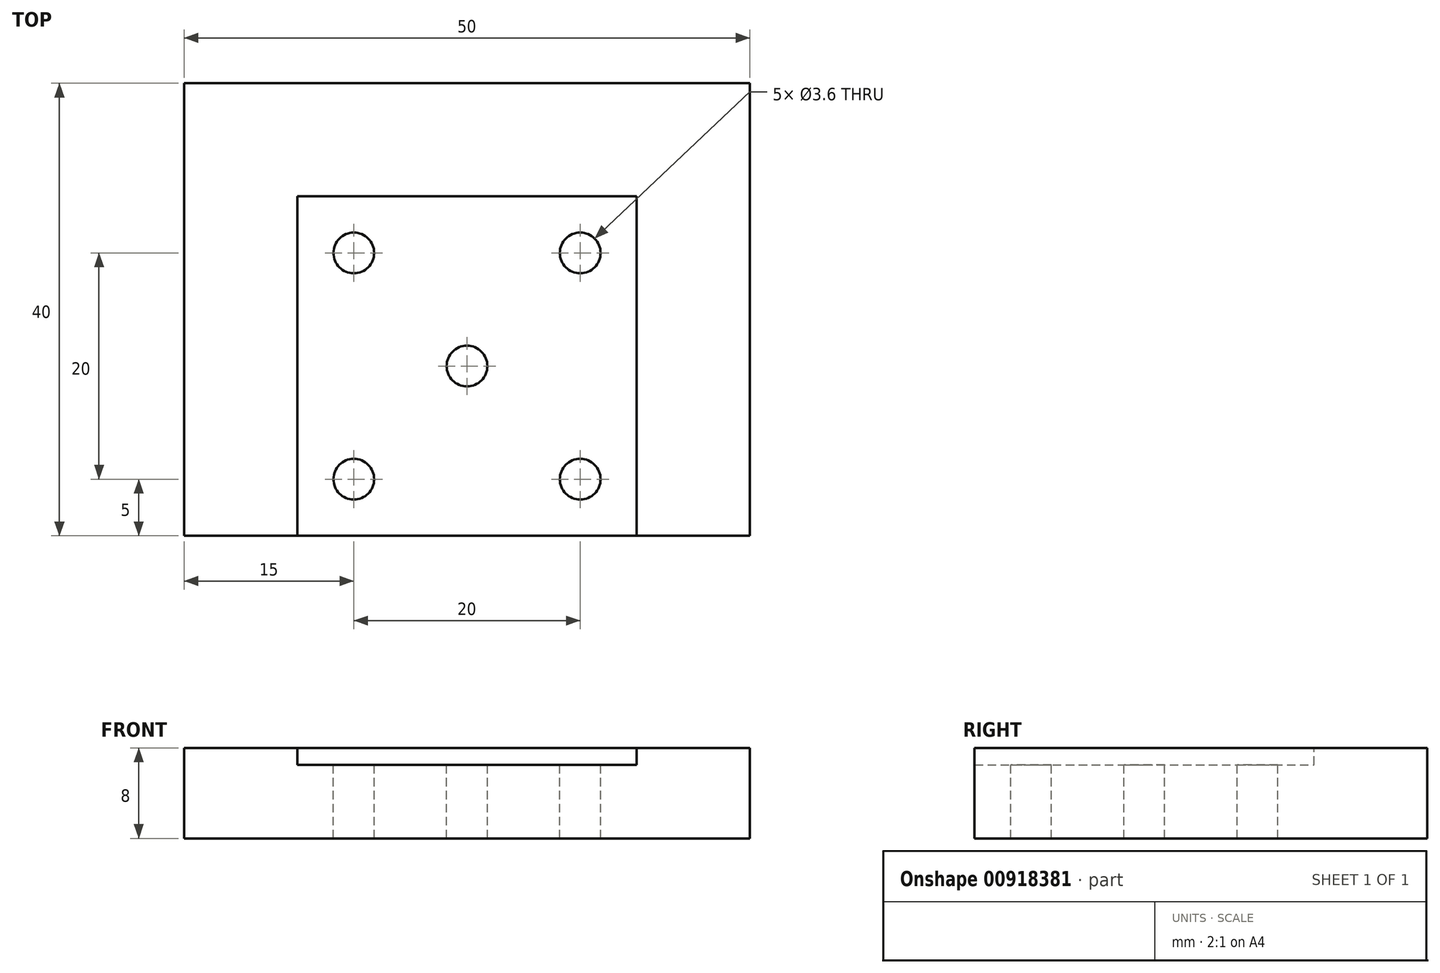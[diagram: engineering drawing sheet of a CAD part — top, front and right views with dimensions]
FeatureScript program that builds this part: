
annotation { "Feature Type Name" : "Feature", "Feature Type Description" : "" }
export const myFeature = defineFeature(function(context is Context, id is Id, definition is map)
    precondition{}
    {
        {
            var Q0;
            Q0=qCreatedBy(makeId("Front.planeOp"),FACE);
            var sketch = newSketch(context, id + "F0", { "sketchPlane" : qUnion([Q0])});
            skCircle(sketch, "E0", {"center": v(0, 18.25) * mm, "radius": 2.85 * mm});
            skCircle(sketch, "E1", {"center": v(0, -18.25) * mm, "radius": 2.85 * mm});
            skCircle(sketch, "E2", {"center": v(0, 0) * mm, "radius": 11 * mm});
            skLineSegment(sketch, "E3", {"start": v(0, 0) * mm, "end": v(0, 18.25) * mm, "construction": true});
            skLineSegment(sketch, "E4", {"start": v(0, -18.25) * mm, "end": v(0, 0) * mm, "construction": true});
            skLineSegment(sketch, "E5.bottom", {"start": v(-15, 28.25) * mm, "end": v(15, 28.25) * mm});
            skLineSegment(sketch, "E5.top", {"start": v(-25, -38.25) * mm, "end": v(25, -38.25) * mm});
            skLineSegment(sketch, "E5.left", {"start": v(-25, 18.25) * mm, "end": v(-25, -38.25) * mm});
            skLineSegment(sketch, "E5.right", {"start": v(25, 18.25) * mm, "end": v(25, -38.25) * mm});
            skLineSegment(sketch, "E6", {"start": v(0, 18.25) * mm, "end": v(0, 28.25) * mm, "construction": true});
            skPoint(sketch, "E7.visualSharp", {"position": v(-25, 28.25) * mm});
            skArc(sketch, "E7.filletArc", {"start": v(-15, 28.25) * mm, "mid": v(-22.07, 25.32) * mm, "end": v(-25, 18.25) * mm});
            skPoint(sketch, "E8.visualSharp", {"position": v(25, 28.25) * mm});
            skArc(sketch, "E8.filletArc", {"start": v(25, 18.25) * mm, "mid": v(22.07, 25.32) * mm, "end": v(15, 28.25) * mm});
            skLineSegment(sketch, "E9", {"start": v(0, 0) * mm, "end": v(25, 0) * mm, "construction": true});
            skSolve(sketch);
        }
        {
            var Q0;
            Q0=makeQuery(id+"F0.imprint","IMPRINT",FACE,{"disambiguationData":[TD([[makeQuery(id+"F0.imprint","IMPRINT",EDGE,{"derivedFrom":sQuery(id+"F0.wireOp",EDGE,"E0")}),-1.0]])]});
            extrude(context, id + "F1", {"entities" : qUnion([Q0]), "depth" : 40 * mm, "offsetDistance" : 25 * mm});
        }
        {
            var Q0;
            Q0=makeQuery(id+"F1.opExtrude","SWEPT_FACE",FACE,{"disambiguationData":[OSD([sQuery(id+"F0.wireOp",EDGE,"E5.bottom")])]});
            var sketch = newSketch(context, id + "F2", { "sketchPlane" : qUnion([Q0])});
            skLineSegment(sketch, "E10.0", {"start": v(-25, -40) * mm, "end": v(-25, 0) * mm, "construction": true});
            skLineSegment(sketch, "E10.1", {"start": v(25, -40) * mm, "end": v(25, 0) * mm, "construction": true});
            skLineSegment(sketch, "E11.bottom", {"start": v(-25, -40) * mm, "end": v(25, -40) * mm});
            skLineSegment(sketch, "E11.top", {"start": v(-25, -10) * mm, "end": v(25, -10) * mm});
            skLineSegment(sketch, "E11.left", {"start": v(-25, -40) * mm, "end": v(-25, -10) * mm});
            skLineSegment(sketch, "E11.right", {"start": v(25, -40) * mm, "end": v(25, -10) * mm});
            skSolve(sketch);
        }
        {
            var Q0;
            {var subQ0=sQuery(id+"F2.wireOp",EDGE,"E11.bottom");var subQ1=sQuery(id+"F0.wireOp",EDGE,"E5.bottom");var subQ2=makeQuery(id+"F1.opExtrude","SWEPT_EDGE",EDGE,{"disambiguationData":[OSD([subQ1,sQuery(id+"F0.wireOp",EDGE,"E7.filletArc")])]});var subQ3=makeQuery(id+"F2.imprint","INTERSECT",VERTEX,{"derivedFrom":[subQ2,subQ0]});Q0=makeQuery(id+"F2.imprint","IMPRINT",FACE,{"disambiguationData":[TD([[makeQuery(id+"F2.imprint","IMPRINT",EDGE,{"disambiguationData":[TD([[subQ3,-1.0]])],"derivedFrom":subQ0}),1.0]])]});}
            extrude(context, id + "F3", {"entities" : qUnion([Q0]), "operationType" : NewBodyOperationType.REMOVE, "oppositeDirection" : true, "depth" : 55 * mm, "offsetDistance" : 25 * mm});
        }
        {
            var Q0;
            Q0=makeQuery(id+"F1.opExtrude","CAP_FACE",FACE,{"disambiguationData":[OSD([sQuery(id+"F0.wireOp",EDGE,"E0"),sQuery(id+"F0.wireOp",EDGE,"E1"),sQuery(id+"F0.wireOp",EDGE,"E2"),sQuery(id+"F0.wireOp",EDGE,"E5.bottom"),sQuery(id+"F0.wireOp",EDGE,"E5.top"),sQuery(id+"F0.wireOp",EDGE,"E5.left"),sQuery(id+"F0.wireOp",EDGE,"E5.right"),sQuery(id+"F0.wireOp",EDGE,"E7.filletArc"),sQuery(id+"F0.wireOp",EDGE,"E8.filletArc")])],"isStart":false});
            var sketch = newSketch(context, id + "F4", { "sketchPlane" : qUnion([Q0])});
            skLineSegment(sketch, "E12.bottom", {"start": v(-15.5, 15.5) * mm, "end": v(15.5, 15.5) * mm, "construction": true});
            skLineSegment(sketch, "E12.top", {"start": v(-15.5, -15.5) * mm, "end": v(15.5, -15.5) * mm, "construction": true});
            skLineSegment(sketch, "E12.left", {"start": v(-15.5, 15.5) * mm, "end": v(-15.5, -15.5) * mm, "construction": true});
            skLineSegment(sketch, "E12.right", {"start": v(15.5, 15.5) * mm, "end": v(15.5, -15.5) * mm, "construction": true});
            skCircle(sketch, "E13", {"center": v(15.5, 15.5) * mm, "radius": 4.5 * mm});
            skCircle(sketch, "E14", {"center": v(-15.5, 15.5) * mm, "radius": 4.5 * mm});
            skCircle(sketch, "E15", {"center": v(-15.5, -15.5) * mm, "radius": 4.5 * mm});
            skCircle(sketch, "E16", {"center": v(15.5, -15.5) * mm, "radius": 4.5 * mm});
            skCircle(sketch, "E17", {"center": v(15.5, 15.5) * mm, "radius": 1.8 * mm});
            skCircle(sketch, "E18", {"center": v(-15.5, 15.5) * mm, "radius": 1.8 * mm});
            skCircle(sketch, "E19", {"center": v(-15.5, -15.5) * mm, "radius": 1.8 * mm});
            skCircle(sketch, "E20", {"center": v(15.5, -15.5) * mm, "radius": 1.8 * mm});
            skSolve(sketch);
        }
        {
            var Q0;
            {var subQ0=sQuery(id+"F4.wireOp",EDGE,"E14");var subQ1=makeQuery(id+"F3.boolean.opBoolean","COPY",EDGE,{"derivedFrom":makeQuery(id+"F3.opExtrude","SWEPT_EDGE",EDGE,{"disambiguationData":[OSD([sQuery(id+"F0.wireOp",EDGE,"E5.bottom"),sQuery(id+"F0.wireOp",EDGE,"E7.filletArc"),sQuery(id+"F2.wireOp",EDGE,"E11.bottom")])]})});var subQ2=makeQuery(id+"F4.imprint","INTERSECT",VERTEX,{"disambiguationData":[OD(0.0)],"derivedFrom":[subQ1,subQ0]});Q0=makeQuery(id+"F4.imprint","IMPRINT",FACE,{"disambiguationData":[TD([[makeQuery(id+"F4.imprint","IMPRINT",EDGE,{"disambiguationData":[TD([[subQ2,1.0]])],"derivedFrom":subQ0}),1.0]])]});}
            var Q1;
            {var subQ0=sQuery(id+"F4.wireOp",EDGE,"E15");var subQ1=makeQuery(id+"F3.boolean.opBoolean","COPY",EDGE,{"derivedFrom":makeQuery(id+"F3.opExtrude","SWEPT_EDGE",EDGE,{"disambiguationData":[OSD([sQuery(id+"F0.wireOp",EDGE,"E5.bottom"),sQuery(id+"F0.wireOp",EDGE,"E7.filletArc"),sQuery(id+"F2.wireOp",EDGE,"E11.bottom")])]})});var subQ2=makeQuery(id+"F4.imprint","INTERSECT",VERTEX,{"disambiguationData":[OD(0.0)],"derivedFrom":[subQ1,subQ0]});Q1=makeQuery(id+"F4.imprint","IMPRINT",FACE,{"disambiguationData":[TD([[makeQuery(id+"F4.imprint","IMPRINT",EDGE,{"disambiguationData":[TD([[subQ2,-1.0]])],"derivedFrom":subQ0}),1.0]])]});}
            var Q2;
            {var subQ0=sQuery(id+"F4.wireOp",EDGE,"E16");var subQ1=makeQuery(id+"F3.boolean.opBoolean","COPY",EDGE,{"derivedFrom":makeQuery(id+"F3.opExtrude","SWEPT_EDGE",EDGE,{"disambiguationData":[OSD([sQuery(id+"F0.wireOp",EDGE,"E5.bottom"),sQuery(id+"F0.wireOp",EDGE,"E8.filletArc"),sQuery(id+"F2.wireOp",EDGE,"E11.bottom")])]})});var subQ2=makeQuery(id+"F4.imprint","INTERSECT",VERTEX,{"disambiguationData":[OD(0.0)],"derivedFrom":[subQ1,subQ0]});Q2=makeQuery(id+"F4.imprint","IMPRINT",FACE,{"disambiguationData":[TD([[makeQuery(id+"F4.imprint","IMPRINT",EDGE,{"disambiguationData":[TD([[subQ2,1.0]])],"derivedFrom":subQ0}),1.0]])]});}
            var Q3;
            {var subQ0=sQuery(id+"F4.wireOp",EDGE,"E13");var subQ1=makeQuery(id+"F3.boolean.opBoolean","COPY",EDGE,{"derivedFrom":makeQuery(id+"F3.opExtrude","SWEPT_EDGE",EDGE,{"disambiguationData":[OSD([sQuery(id+"F0.wireOp",EDGE,"E5.bottom"),sQuery(id+"F0.wireOp",EDGE,"E8.filletArc"),sQuery(id+"F2.wireOp",EDGE,"E11.bottom")])]})});var subQ2=makeQuery(id+"F4.imprint","INTERSECT",VERTEX,{"disambiguationData":[OD(0.0)],"derivedFrom":[subQ1,subQ0]});Q3=makeQuery(id+"F4.imprint","IMPRINT",FACE,{"disambiguationData":[TD([[makeQuery(id+"F4.imprint","IMPRINT",EDGE,{"disambiguationData":[TD([[subQ2,-1.0]])],"derivedFrom":subQ0}),1.0]])]});}
            var Q4;
            Q4=makeQuery(id+"F3.boolean.opBoolean","COPY",VERTEX,{"derivedFrom":makeQuery(id+"F3.opExtrude","CAP_VERTEX",VERTEX,{"disambiguationData":[OSD([sQuery(id+"F0.wireOp",EDGE,"E5.bottom"),sQuery(id+"F0.wireOp",EDGE,"E7.filletArc"),sQuery(id+"F2.wireOp",EDGE,"E11.top")])],"isStart":true})});
            extrude(context, id + "F5", {"entities" : qUnion([Q0, Q1, Q2, Q3]), "operationType" : NewBodyOperationType.ADD, "endBound" : BoundingType.UP_TO_VERTEX, "oppositeDirection" : true, "depth" : 25 * mm, "endBoundEntityVertex" : qUnion([Q4]), "offsetDistance" : 25 * mm});
        }
        {
            var Q0;
            {var subQ0=sQuery(id+"F4.wireOp",EDGE,"E18");var subQ1=makeQuery(id+"F3.boolean.opBoolean","COPY",EDGE,{"derivedFrom":makeQuery(id+"F3.opExtrude","SWEPT_EDGE",EDGE,{"disambiguationData":[OSD([sQuery(id+"F0.wireOp",EDGE,"E5.bottom"),sQuery(id+"F0.wireOp",EDGE,"E7.filletArc"),sQuery(id+"F2.wireOp",EDGE,"E11.bottom")])]})});var subQ2=makeQuery(id+"F4.imprint","INTERSECT",VERTEX,{"disambiguationData":[OD(0.0)],"derivedFrom":[subQ1,subQ0]});Q0=makeQuery(id+"F4.imprint","IMPRINT",FACE,{"disambiguationData":[TD([[makeQuery(id+"F4.imprint","IMPRINT",EDGE,{"disambiguationData":[TD([[subQ2,-1.0]])],"derivedFrom":subQ0}),1.0]])]});}
            var Q1;
            {var subQ0=sQuery(id+"F4.wireOp",EDGE,"E17");var subQ1=makeQuery(id+"F3.boolean.opBoolean","COPY",EDGE,{"derivedFrom":makeQuery(id+"F3.opExtrude","SWEPT_EDGE",EDGE,{"disambiguationData":[OSD([sQuery(id+"F0.wireOp",EDGE,"E5.bottom"),sQuery(id+"F0.wireOp",EDGE,"E8.filletArc"),sQuery(id+"F2.wireOp",EDGE,"E11.bottom")])]})});var subQ2=makeQuery(id+"F4.imprint","INTERSECT",VERTEX,{"disambiguationData":[OD(0.0)],"derivedFrom":[subQ1,subQ0]});Q1=makeQuery(id+"F4.imprint","IMPRINT",FACE,{"disambiguationData":[TD([[makeQuery(id+"F4.imprint","IMPRINT",EDGE,{"disambiguationData":[TD([[subQ2,1.0]])],"derivedFrom":subQ0}),1.0]])]});}
            var Q2;
            {var subQ0=sQuery(id+"F4.wireOp",EDGE,"E20");var subQ1=makeQuery(id+"F3.boolean.opBoolean","COPY",EDGE,{"derivedFrom":makeQuery(id+"F3.opExtrude","SWEPT_EDGE",EDGE,{"disambiguationData":[OSD([sQuery(id+"F0.wireOp",EDGE,"E5.bottom"),sQuery(id+"F0.wireOp",EDGE,"E8.filletArc"),sQuery(id+"F2.wireOp",EDGE,"E11.bottom")])]})});var subQ2=makeQuery(id+"F4.imprint","INTERSECT",VERTEX,{"disambiguationData":[OD(0.0)],"derivedFrom":[subQ1,subQ0]});Q2=makeQuery(id+"F4.imprint","IMPRINT",FACE,{"disambiguationData":[TD([[makeQuery(id+"F4.imprint","IMPRINT",EDGE,{"disambiguationData":[TD([[subQ2,-1.0]])],"derivedFrom":subQ0}),1.0]])]});}
            var Q3;
            {var subQ0=sQuery(id+"F4.wireOp",EDGE,"E19");var subQ1=makeQuery(id+"F3.boolean.opBoolean","COPY",EDGE,{"derivedFrom":makeQuery(id+"F3.opExtrude","SWEPT_EDGE",EDGE,{"disambiguationData":[OSD([sQuery(id+"F0.wireOp",EDGE,"E5.bottom"),sQuery(id+"F0.wireOp",EDGE,"E7.filletArc"),sQuery(id+"F2.wireOp",EDGE,"E11.bottom")])]})});var subQ2=makeQuery(id+"F4.imprint","INTERSECT",VERTEX,{"disambiguationData":[OD(0.0)],"derivedFrom":[subQ1,subQ0]});Q3=makeQuery(id+"F4.imprint","IMPRINT",FACE,{"disambiguationData":[TD([[makeQuery(id+"F4.imprint","IMPRINT",EDGE,{"disambiguationData":[TD([[subQ2,1.0]])],"derivedFrom":subQ0}),1.0]])]});}
            extrude(context, id + "F6", {"entities" : qUnion([Q0, Q1, Q2, Q3]), "operationType" : NewBodyOperationType.REMOVE, "endBound" : BoundingType.THROUGH_ALL, "oppositeDirection" : true, "depth" : 25 * mm, "offsetDistance" : 25 * mm});
        }
        {
            var Q0;
            {var subQ0=sQuery(id+"F4.wireOp",EDGE,"E18");var subQ1=makeQuery(id+"F3.boolean.opBoolean","COPY",EDGE,{"derivedFrom":makeQuery(id+"F3.opExtrude","SWEPT_EDGE",EDGE,{"disambiguationData":[OSD([sQuery(id+"F0.wireOp",EDGE,"E5.bottom"),sQuery(id+"F0.wireOp",EDGE,"E7.filletArc"),sQuery(id+"F2.wireOp",EDGE,"E11.bottom")])]})});var subQ2=makeQuery(id+"F4.imprint","INTERSECT",VERTEX,{"disambiguationData":[OD(0.0)],"derivedFrom":[subQ1,subQ0]});Q0=makeQuery(id+"F4.imprint","IMPRINT",FACE,{"disambiguationData":[TD([[makeQuery(id+"F4.imprint","IMPRINT",EDGE,{"disambiguationData":[TD([[subQ2,1.0]])],"derivedFrom":subQ0}),1.0]])]});}
            var Q1;
            {var subQ0=sQuery(id+"F4.wireOp",EDGE,"E17");var subQ1=makeQuery(id+"F3.boolean.opBoolean","COPY",EDGE,{"derivedFrom":makeQuery(id+"F3.opExtrude","SWEPT_EDGE",EDGE,{"disambiguationData":[OSD([sQuery(id+"F0.wireOp",EDGE,"E5.bottom"),sQuery(id+"F0.wireOp",EDGE,"E8.filletArc"),sQuery(id+"F2.wireOp",EDGE,"E11.bottom")])]})});var subQ2=makeQuery(id+"F4.imprint","INTERSECT",VERTEX,{"disambiguationData":[OD(0.0)],"derivedFrom":[subQ1,subQ0]});Q1=makeQuery(id+"F4.imprint","IMPRINT",FACE,{"disambiguationData":[TD([[makeQuery(id+"F4.imprint","IMPRINT",EDGE,{"disambiguationData":[TD([[subQ2,-1.0]])],"derivedFrom":subQ0}),1.0]])]});}
            var Q2;
            {var subQ0=sQuery(id+"F4.wireOp",EDGE,"E19");var subQ1=makeQuery(id+"F3.boolean.opBoolean","COPY",EDGE,{"derivedFrom":makeQuery(id+"F3.opExtrude","SWEPT_EDGE",EDGE,{"disambiguationData":[OSD([sQuery(id+"F0.wireOp",EDGE,"E5.bottom"),sQuery(id+"F0.wireOp",EDGE,"E7.filletArc"),sQuery(id+"F2.wireOp",EDGE,"E11.bottom")])]})});var subQ2=makeQuery(id+"F4.imprint","INTERSECT",VERTEX,{"disambiguationData":[OD(0.0)],"derivedFrom":[subQ1,subQ0]});Q2=makeQuery(id+"F4.imprint","IMPRINT",FACE,{"disambiguationData":[TD([[makeQuery(id+"F4.imprint","IMPRINT",EDGE,{"disambiguationData":[TD([[subQ2,-1.0]])],"derivedFrom":subQ0}),1.0]])]});}
            var Q3;
            {var subQ0=sQuery(id+"F4.wireOp",EDGE,"E20");var subQ1=makeQuery(id+"F3.boolean.opBoolean","COPY",EDGE,{"derivedFrom":makeQuery(id+"F3.opExtrude","SWEPT_EDGE",EDGE,{"disambiguationData":[OSD([sQuery(id+"F0.wireOp",EDGE,"E5.bottom"),sQuery(id+"F0.wireOp",EDGE,"E8.filletArc"),sQuery(id+"F2.wireOp",EDGE,"E11.bottom")])]})});var subQ2=makeQuery(id+"F4.imprint","INTERSECT",VERTEX,{"disambiguationData":[OD(0.0)],"derivedFrom":[subQ1,subQ0]});Q3=makeQuery(id+"F4.imprint","IMPRINT",FACE,{"disambiguationData":[TD([[makeQuery(id+"F4.imprint","IMPRINT",EDGE,{"disambiguationData":[TD([[subQ2,1.0]])],"derivedFrom":subQ0}),1.0]])]});}
            extrude(context, id + "F7", {"entities" : qUnion([Q0, Q1, Q2, Q3]), "operationType" : NewBodyOperationType.REMOVE, "endBound" : BoundingType.THROUGH_ALL, "oppositeDirection" : true, "depth" : 25 * mm, "offsetDistance" : 25 * mm});
        }
        {
            var Q0;
            Q0=makeQuery(id+"F3.boolean.opBoolean","COPY",FACE,{"derivedFrom":makeQuery(id+"F3.opExtrude","CAP_FACE",FACE,{"disambiguationData":[OSD([sQuery(id+"F0.wireOp",EDGE,"E5.bottom"),sQuery(id+"F0.wireOp",EDGE,"E7.filletArc"),sQuery(id+"F0.wireOp",EDGE,"E8.filletArc"),sQuery(id+"F2.wireOp",EDGE,"E11.bottom"),sQuery(id+"F2.wireOp",EDGE,"E11.top")])],"isStart":false})});
            var sketch = newSketch(context, id + "F8", { "sketchPlane" : qUnion([Q0])});
            skLineSegment(sketch, "E21.bottom", {"start": v(-10, -15) * mm, "end": v(10, -15) * mm, "construction": true});
            skLineSegment(sketch, "E21.top", {"start": v(-10, -35) * mm, "end": v(10, -35) * mm, "construction": true});
            skLineSegment(sketch, "E21.left", {"start": v(-10, -15) * mm, "end": v(-10, -35) * mm, "construction": true});
            skLineSegment(sketch, "E21.right", {"start": v(10, -15) * mm, "end": v(10, -35) * mm, "construction": true});
            skLineSegment(sketch, "E22", {"start": v(-15, -25) * mm, "end": v(15, -25) * mm, "construction": true});
            skCircle(sketch, "E23", {"center": v(-10, -15) * mm, "radius": 1.8 * mm});
            skCircle(sketch, "E24", {"center": v(10, -15) * mm, "radius": 1.8 * mm});
            skCircle(sketch, "E25", {"center": v(-10, -35) * mm, "radius": 1.8 * mm});
            skCircle(sketch, "E26", {"center": v(10, -35) * mm, "radius": 1.8 * mm});
            skCircle(sketch, "E27", {"center": v(0, -25) * mm, "radius": 1.8 * mm});
            skSolve(sketch);
        }
        {
            var Q0;
            Q0=qSketchRegion(id+"F8",true);
            var Q1;
            Q1=makeQuery(id+"F1.opExtrude","SWEPT_FACE",FACE,{"disambiguationData":[OSD([sQuery(id+"F0.wireOp",EDGE,"E5.top")])]});
            extrude(context, id + "F9", {"entities" : qUnion([Q0]), "operationType" : NewBodyOperationType.REMOVE, "endBound" : BoundingType.UP_TO_SURFACE, "oppositeDirection" : true, "depth" : 25 * mm, "endBoundEntityFace" : qUnion([Q1]), "offsetDistance" : 25 * mm});
        }
        {
            var Q0;
            Q0=makeQuery(id+"F1.opExtrude","SWEPT_FACE",FACE,{"disambiguationData":[OSD([sQuery(id+"F0.wireOp",EDGE,"E5.top")])]});
            extrude(context, id + "F10", {"entities" : qUnion([Q0]), "operationType" : NewBodyOperationType.INTERSECT, "oppositeDirection" : true, "depth" : 13 * mm, "offsetDistance" : 25 * mm});
        }
        {
            var Q0;
            Q0=makeQuery(id+"F1.opExtrude","SWEPT_FACE",FACE,{"disambiguationData":[OSD([sQuery(id+"F0.wireOp",EDGE,"E5.top")])]});
            extrude(context, id + "F11", {"entities" : qUnion([Q0]), "operationType" : NewBodyOperationType.REMOVE, "oppositeDirection" : true, "depth" : 5 * mm, "offsetDistance" : 25 * mm});
        }
    });
